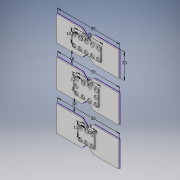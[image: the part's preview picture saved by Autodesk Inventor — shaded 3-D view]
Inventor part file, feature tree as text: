
AUTODESK INVENTOR PART (.ipt)
format: ipt  version: 2017 (Build 210142000, 142)  size: 299,520 bytes
history: native  units: in
note: dims shown in document units (in); Inventor stores cm internally (conversion verified against a paired STEP export)
features: extrude x2, sketch x1
ambient origin geometry x8: Origin, YZ Plane, XZ Plane, XY Plane, X Axis, Y Axis, Z Axis, Center Point
bodies: Solid1 (feature_tree)
feature tree (3):
  sketch  "Sketch1"  dims[d1=1.9685in d2=0.748in d3=0.5118in d12=0.125in d14=1.9685in d15=0.4921in d16=0.4449in d17=0.125in d18=0.7874in d19=1.9685in d20=0.8957in d21=0.4232in d22=0.125in d23=0.3937in d24=0.3937in d25=0.0394in d26=0.0in d27=0.0787in d28=0.0in]
  extrude  "Extrusion1"  Depth=0.748in
  extrude  "Extrusion2"  Depth=0.5118in
